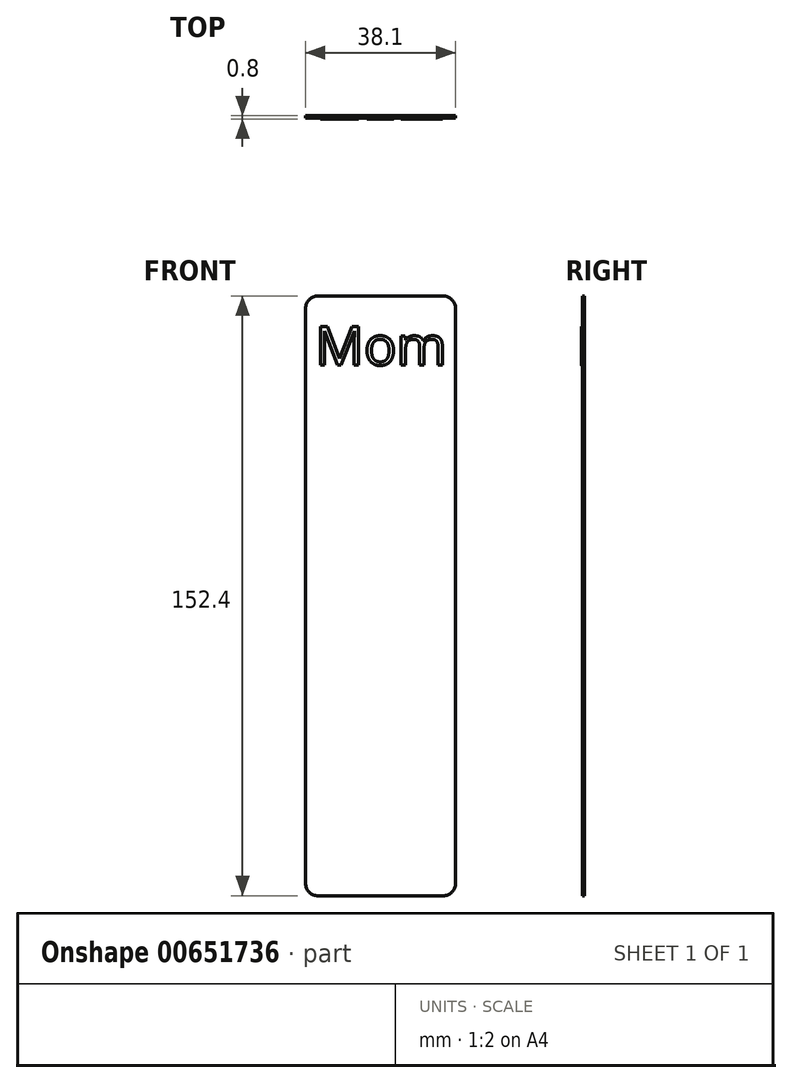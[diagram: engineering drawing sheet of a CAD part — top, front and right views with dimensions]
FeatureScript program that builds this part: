
annotation { "Feature Type Name" : "Feature", "Feature Type Description" : "" }
export const myFeature = defineFeature(function(context is Context, id is Id, definition is map)
    precondition{}
    {
        {
            var Q0;
            Q0=qCreatedBy(makeId("Front.planeOp"),FACE);
            var sketch = newSketch(context, id + "F0", { "sketchPlane" : qUnion([Q0])});
            skLineSegment(sketch, "E0.bottom", {"start": v(3.18, 0) * mm, "end": v(34.93, 0) * mm});
            skLineSegment(sketch, "E0.top", {"start": v(3.18, -152.4) * mm, "end": v(34.93, -152.4) * mm});
            skLineSegment(sketch, "E0.left", {"start": v(0, -3.17) * mm, "end": v(0, -149.22) * mm});
            skLineSegment(sketch, "E0.right", {"start": v(38.1, -3.17) * mm, "end": v(38.1, -149.22) * mm});
            skPoint(sketch, "E1.visualSharp", {"position": v(0, 0) * mm});
            skArc(sketch, "E1.filletArc", {"start": v(3.18, 0) * mm, "mid": v(0.93, -0.93) * mm, "end": v(0, -3.18) * mm});
            skPoint(sketch, "E2.visualSharp", {"position": v(38.1, 0) * mm});
            skArc(sketch, "E2.filletArc", {"start": v(38.1, -3.18) * mm, "mid": v(37.17, -0.93) * mm, "end": v(34.93, 0) * mm});
            skPoint(sketch, "E3.visualSharp", {"position": v(38.1, -152.4) * mm});
            skArc(sketch, "E3.filletArc", {"start": v(34.93, -152.4) * mm, "mid": v(37.17, -151.47) * mm, "end": v(38.1, -149.22) * mm});
            skPoint(sketch, "E4.visualSharp", {"position": v(0, -152.4) * mm});
            skArc(sketch, "E4.filletArc", {"start": v(0, -149.22) * mm, "mid": v(0.93, -151.47) * mm, "end": v(3.18, -152.4) * mm});
            skSolve(sketch);
        }
        {
            var Q0;
            Q0 = qSketchRegion(id + "F0", true);
            extrude(context, id + "F1", {"entities" : qUnion([Q0]), "depth" : .6 * mm, "offsetDistance" : 25.4 * mm});
        }
        {
            var Q0;
            Q0=makeQuery(id+"F1.opExtrude","CAP_FACE",FACE,{"disambiguationData":[OSD([sQuery(id+"F0.wireOp",EDGE,"E0.bottom"),sQuery(id+"F0.wireOp",EDGE,"E0.top"),sQuery(id+"F0.wireOp",EDGE,"E0.left"),sQuery(id+"F0.wireOp",EDGE,"E0.right"),sQuery(id+"F0.wireOp",EDGE,"E1.filletArc"),sQuery(id+"F0.wireOp",EDGE,"E2.filletArc"),sQuery(id+"F0.wireOp",EDGE,"E3.filletArc"),sQuery(id+"F0.wireOp",EDGE,"E4.filletArc")])],"isStart":false});
            var sketch = newSketch(context, id + "F2", { "sketchPlane" : qUnion([Q0])});
            skText(sketch, "E5", { "text": "Mom", "fontName": "OpenSans-Regular.ttf"});
            const initialGuessF2  = {"E5": [0.00246, -0.01755, 1, 0, 0.00987]};
            skSetInitialGuess(sketch, initialGuessF2);
            skSolve(sketch);
        }
        {
            var Q0;
            Q0 = qSketchRegion(id + "F2", true);
            extrude(context, id + "F3", {"entities" : qUnion([Q0]), "operationType" : NewBodyOperationType.ADD, "depth" : .2 * mm, "offsetDistance" : 25.4 * mm});
        }
    });
